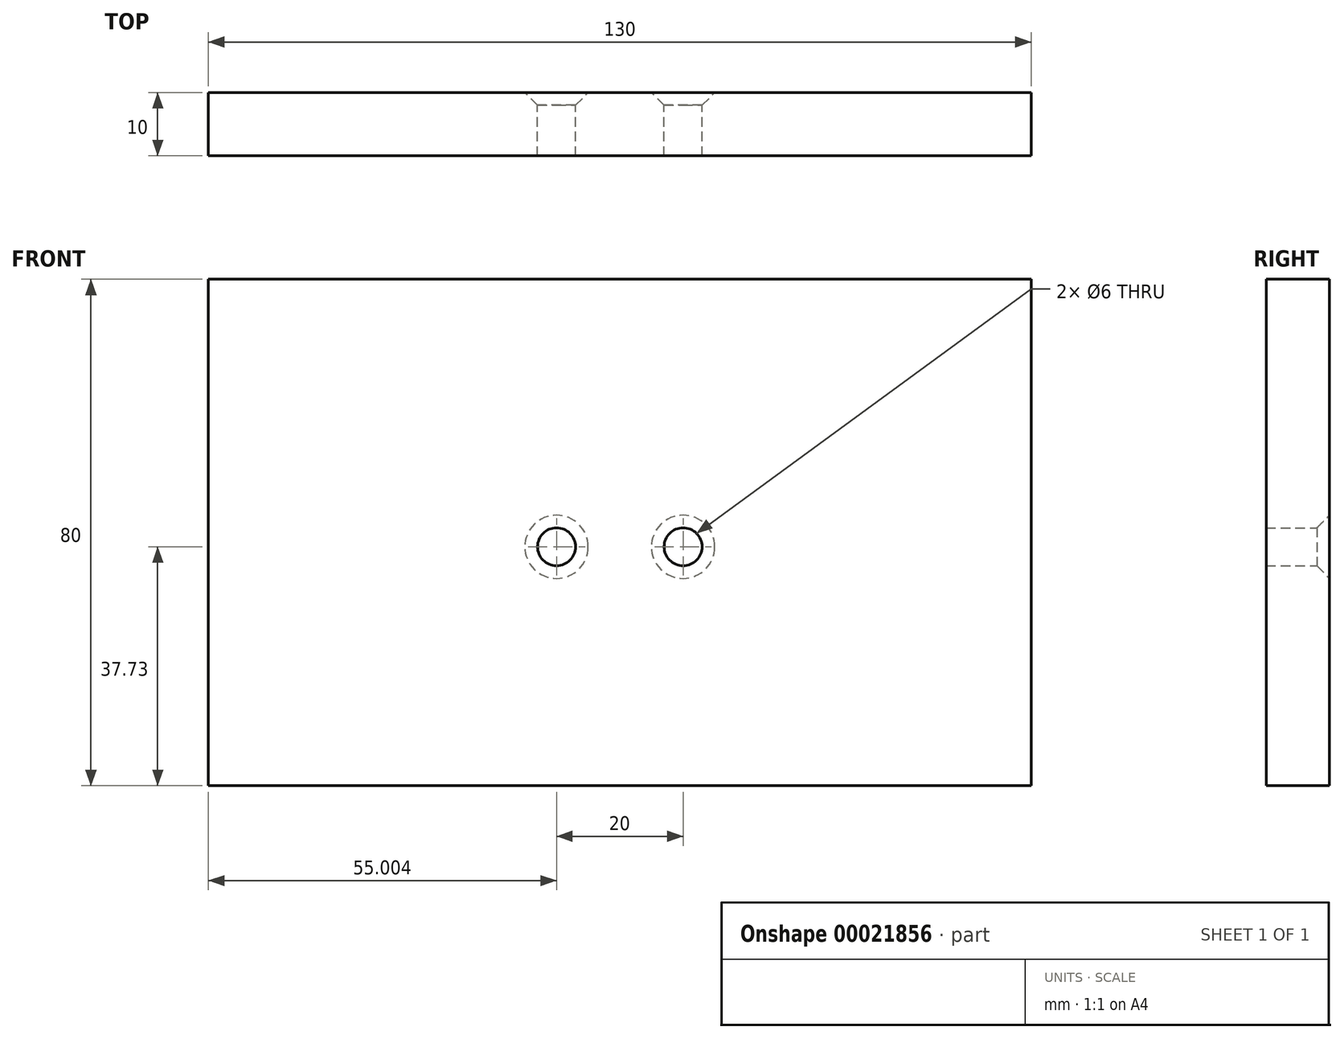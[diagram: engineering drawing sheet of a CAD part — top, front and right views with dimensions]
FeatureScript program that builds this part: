
annotation { "Feature Type Name" : "Feature", "Feature Type Description" : "" }
export const myFeature = defineFeature(function(context is Context, id is Id, definition is map)
    precondition{}
    {
        {
            var Q0;
            Q0=qCreatedBy(makeId("Front.planeOp"),FACE);
            var sketch = newSketch(context, id + "F0", { "sketchPlane" : qUnion([Q0])});
            skLineSegment(sketch, "E0.bottom", {"start": v(-59.57, 42.27) * mm, "end": v(70.43, 42.27) * mm});
            skLineSegment(sketch, "E0.top", {"start": v(-59.57, -37.73) * mm, "end": v(70.43, -37.73) * mm});
            skLineSegment(sketch, "E0.left", {"start": v(-59.57, 42.27) * mm, "end": v(-59.57, -37.73) * mm});
            skLineSegment(sketch, "E0.right", {"start": v(70.43, 42.27) * mm, "end": v(70.43, -37.73) * mm});
            skSolve(sketch);
        }
        {
            var Q0;
            Q0=makeQuery(id+"F0.imprint","IMPRINT",FACE,{"disambiguationData":[TD([[makeQuery(id+"F0.imprint","IMPRINT",EDGE,{"derivedFrom":sQuery(id+"F0.wireOp",EDGE,"E0.bottom")}),-1.0]])]});
            extrude(context, id + "F1", {"entities" : qUnion([Q0]), "depth" : 10 * mm});
        }
        {
            var Q0;
            Q0=makeQuery(id+"F1.opExtrude","CAP_FACE",FACE,{"disambiguationData":[OSD([sQuery(id+"F0.wireOp",EDGE,"E0.bottom"),sQuery(id+"F0.wireOp",EDGE,"E0.top"),sQuery(id+"F0.wireOp",EDGE,"E0.left"),sQuery(id+"F0.wireOp",EDGE,"E0.right")])],"isStart":true});
            var sketch = newSketch(context, id + "F2", { "sketchPlane" : qUnion([Q0])});
            skPoint(sketch, "E1", {"position": v(4.57, 0) * mm});
            skPoint(sketch, "E2", {"position": v(-15.43, 0) * mm});
            skSolve(sketch);
        }
        {
            var Q0;
            Q0=sQuery(id+"F2.wireOp",VERTEX,"E1");
            var Q1;
            Q1=sQuery(id+"F2.wireOp",VERTEX,"E2");
            var Q2;
            Q2=makeQuery(id+"F1.opExtrude","SWEPT_BODY",BODY,{"disambiguationData":[OSD([sQuery(id+"F0.wireOp",EDGE,"E0.bottom"),sQuery(id+"F0.wireOp",EDGE,"E0.top"),sQuery(id+"F0.wireOp",EDGE,"E0.left"),sQuery(id+"F0.wireOp",EDGE,"E0.right")])]});
            hole(context, id + "F3", {"style" : HoleStyle.C_SINK, "holeDiameter" : 6 * mm, "cSinkDiameter" : 10 * mm, "endStyle" : HoleEndStyle.THROUGH, "locations" : qUnion([Q0, Q1]), "scope" : qUnion([Q2]), "cSinkAngle" : 90 * degree});
        }
    });
